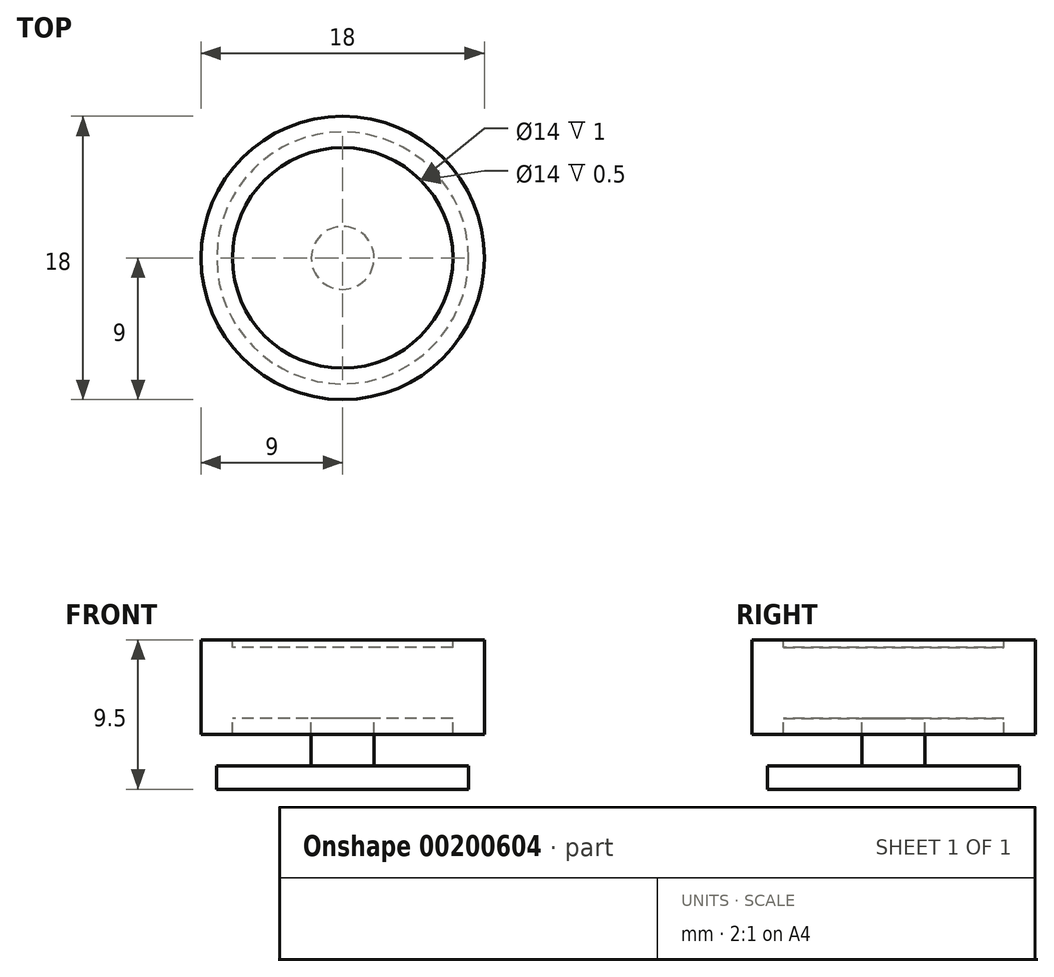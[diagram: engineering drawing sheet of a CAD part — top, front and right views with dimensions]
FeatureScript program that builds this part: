
annotation { "Feature Type Name" : "Feature", "Feature Type Description" : "" }
export const myFeature = defineFeature(function(context is Context, id is Id, definition is map)
    precondition{}
    {
        {
            var Q0;
            Q0=qCreatedBy(makeId("Front.planeOp"),FACE);
            var sketch = newSketch(context, id + "F0", { "sketchPlane" : qUnion([Q0])});
            skLineSegment(sketch, "E0", {"start": v(0, 0) * mm, "end": v(8, 0) * mm});
            skLineSegment(sketch, "E1", {"start": v(8, 0) * mm, "end": v(8, 1.5) * mm});
            skLineSegment(sketch, "E2", {"start": v(8, 1.5) * mm, "end": v(0, 1.5) * mm});
            skLineSegment(sketch, "E3", {"start": v(0, 1.5) * mm, "end": v(2, 1.5) * mm});
            skLineSegment(sketch, "E4", {"start": v(2, 1.5) * mm, "end": v(2, 4.5) * mm});
            skLineSegment(sketch, "E5", {"start": v(2, 4.5) * mm, "end": v(7, 4.5) * mm});
            skLineSegment(sketch, "E6", {"start": v(7, 4.5) * mm, "end": v(7, 3.5) * mm});
            skLineSegment(sketch, "E7", {"start": v(7, 3.5) * mm, "end": v(9, 3.5) * mm});
            skLineSegment(sketch, "E8", {"start": v(9, 3.5) * mm, "end": v(9, 9.5) * mm});
            skLineSegment(sketch, "E9", {"start": v(9, 9.5) * mm, "end": v(7, 9.5) * mm});
            skLineSegment(sketch, "E10", {"start": v(7, 9.5) * mm, "end": v(7, 9) * mm});
            skLineSegment(sketch, "E11", {"start": v(7, 9) * mm, "end": v(0, 9) * mm});
            skLineSegment(sketch, "E12", {"start": v(0, 9) * mm, "end": v(0, 0) * mm});
            skSolve(sketch);
        }
        {
            var Q0;
            Q0 = qSketchRegion(id + "F0", true);
            var Q1;
            Q1=sQuery(id+"F0.wireOp",EDGE,"E12");
            revolve(context, id + "F1", {"entities" : qUnion([Q0]), "axis" : qUnion([Q1]), "revolveType" : RevolveType.FULL});
        }
    });
